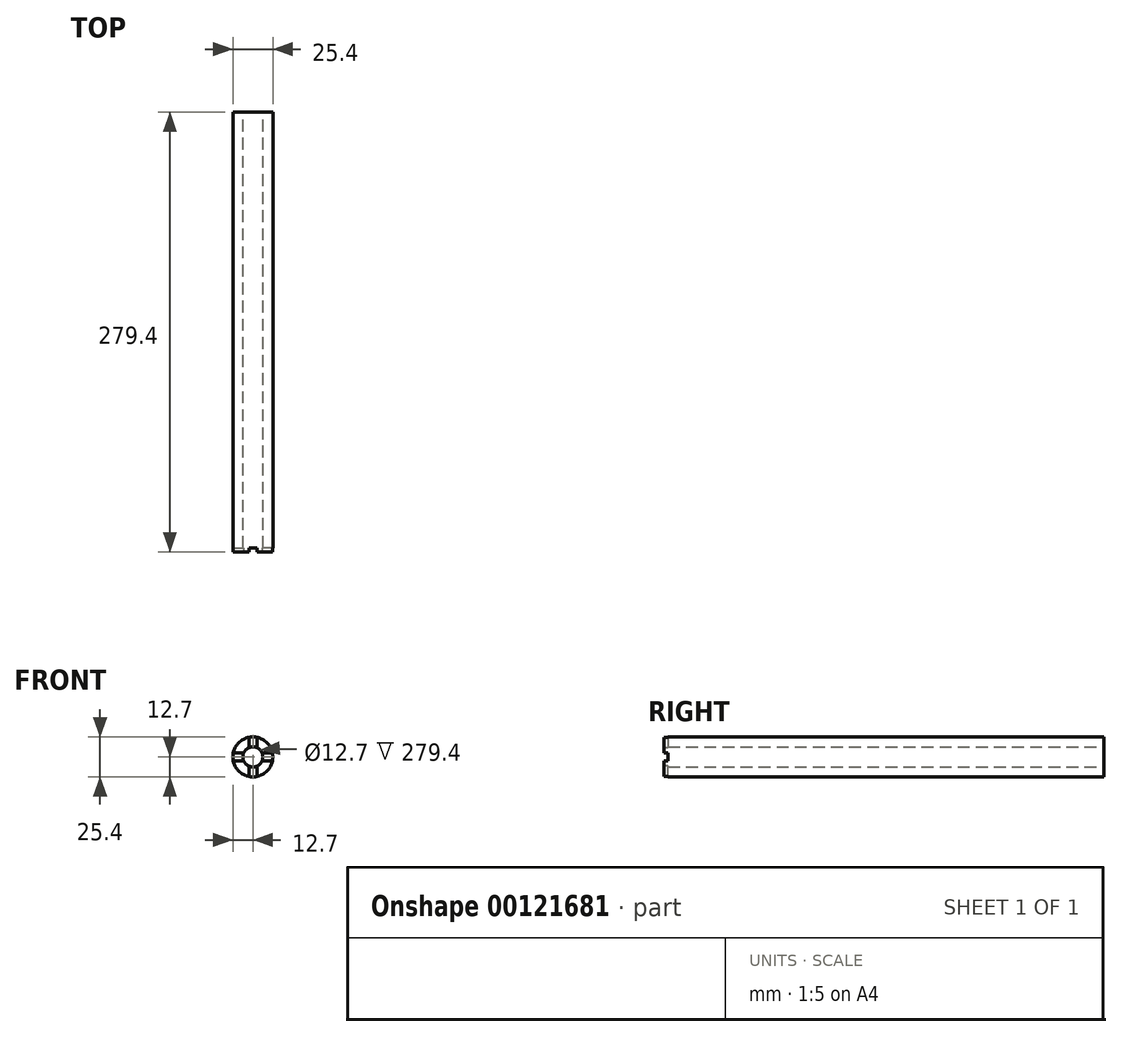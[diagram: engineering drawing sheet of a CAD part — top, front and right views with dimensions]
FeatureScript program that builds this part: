
annotation { "Feature Type Name" : "Feature", "Feature Type Description" : "" }
export const myFeature = defineFeature(function(context is Context, id is Id, definition is map)
    precondition{}
    {
        {
            var Q0;
            Q0=qCreatedBy(makeId("Front.planeOp"),FACE);
            var sketch = newSketch(context, id + "F0", { "sketchPlane" : qUnion([Q0])});
            skCircle(sketch, "E0", {"center": v(0, 0) * mm, "radius": 12.7 * mm});
            skCircle(sketch, "E1", {"center": v(0, 0) * mm, "radius": 6.35 * mm});
            skSolve(sketch);
        }
        {
            var Q0;
            Q0=makeQuery(id+"F0.imprint","IMPRINT",FACE,{"disambiguationData":[TD([[makeQuery(id+"F0.imprint","IMPRINT",EDGE,{"derivedFrom":sQuery(id+"F0.wireOp",EDGE,"E0")}),1.0]])]});
            extrude(context, id + "F1", {"entities" : qUnion([Q0]), "depth" : 279.4 * mm});
        }
        {
            var Q0;
            Q0=makeQuery(id+"F1.opExtrude","CAP_FACE",FACE,{"disambiguationData":[OSD([sQuery(id+"F0.wireOp",EDGE,"E0"),sQuery(id+"F0.wireOp",EDGE,"E1")])],"isStart":false});
            var sketch = newSketch(context, id + "F2", { "sketchPlane" : qUnion([Q0])});
            skCircle(sketch, "E2", {"center": v(0, 0) * mm, "radius": 12.7 * mm});
            skCircle(sketch, "E3", {"center": v(0, 0) * mm, "radius": 6.35 * mm});
            skLineSegment(sketch, "E4", {"start": v(-2.54, 12.44) * mm, "end": v(-2.54, 5.82) * mm});
            skLineSegment(sketch, "E5", {"start": v(-12.44, 2.54) * mm, "end": v(-5.82, 2.54) * mm});
            skLineSegment(sketch, "E6.MirrorCS", {"start": v(2.54, 12.44) * mm, "end": v(2.54, 5.82) * mm});
            skLineSegment(sketch, "E7.MirrorCS", {"start": v(-12.44, -2.54) * mm, "end": v(-5.82, -2.54) * mm});
            skLineSegment(sketch, "E8.MirrorCS", {"start": v(-2.54, -12.44) * mm, "end": v(-2.54, -5.82) * mm});
            skLineSegment(sketch, "E9.MirrorCS", {"start": v(2.54, -12.44) * mm, "end": v(2.54, -5.82) * mm});
            skLineSegment(sketch, "E10.MirrorCS", {"start": v(12.44, 2.54) * mm, "end": v(5.82, 2.54) * mm});
            skLineSegment(sketch, "E11.MirrorCS", {"start": v(12.44, -2.54) * mm, "end": v(5.82, -2.54) * mm});
            skSolve(sketch);
        }
        {
            var Q0;
            {var subQ0=sQuery(id+"F2.wireOp",EDGE,"E4");Q0=makeQuery(id+"F2.imprint","IMPRINT",FACE,{"disambiguationData":[TD([[makeQuery(id+"F2.imprint","IMPRINT",EDGE,{"derivedFrom":subQ0}),1.0]])]});}
            var Q1;
            {var subQ0=sQuery(id+"F2.wireOp",EDGE,"E5");Q1=makeQuery(id+"F2.imprint","IMPRINT",FACE,{"disambiguationData":[TD([[makeQuery(id+"F2.imprint","IMPRINT",EDGE,{"derivedFrom":subQ0}),-1.0]])]});}
            var Q2;
            {var subQ0=sQuery(id+"F2.wireOp",EDGE,"E8.MirrorCS");Q2=makeQuery(id+"F2.imprint","IMPRINT",FACE,{"disambiguationData":[TD([[makeQuery(id+"F2.imprint","IMPRINT",EDGE,{"derivedFrom":subQ0}),-1.0]])]});}
            var Q3;
            {var subQ0=sQuery(id+"F2.wireOp",EDGE,"E10.MirrorCS");Q3=makeQuery(id+"F2.imprint","IMPRINT",FACE,{"disambiguationData":[TD([[makeQuery(id+"F2.imprint","IMPRINT",EDGE,{"derivedFrom":subQ0}),1.0]])]});}
            extrude(context, id + "F3", {"entities" : qUnion([Q0, Q1, Q2, Q3]), "operationType" : NewBodyOperationType.REMOVE, "oppositeDirection" : true, "depth" : 2.54 * mm});
        }
    });
